# Revit family: PRD_AR_FlshCntrlDvcs_F5EElectronicWCFlush_F5EF4004
name_source: partatom
category: Plumbing Fixtures
units: mm (PartAtom-declared; Revit-internal decimal feet)

## family parameters
Cut with Voids When Loaded = Yes
Enable Cutting in Views = Yes
Host = Face
Maintain Annotation Orientation = No
OmniClass Number = 23.45.55.11
OmniClass Title = Sanitary Components
Part Type = Normal
Room Calculation Point = No
Round Connector Dimension = Use Diameter
Shared = No

## types (1)
- F5EF4004
    AssetType = Fixed
    BIMObjectName = PRD_AR_FlushControlDevices_F5EElectronicWCFlush_F5EF4004
    BasicColour = stainless steel-look
    BodyMaterial = PRD_AR_StainlessSteel_Brushed
    ButtonMaterial = PRD_AR_ChromatedBrass_HighPolished
    CW Connection = Yes
    CWFU = 0
    Category = Pr_75_50_46_31, Flush control devices
    Color = stainless steel-look
    Default Elevation = 1219 mm
    DefaultAutomaticHygieneFlush = 24h after the last activity
    Description = F5E - A3000 open WC flush valve for concealed mounting, electronically controlled. Especially suitable for facilities at risk of vandalism. With waterproof electronic module with additional input for sensors to be provided by the client, maximum distance to the electronic module 5 m, solenoid flush valve including enclosed throttle insert for reducing flush volume, waterproof electrical T-junction for connection to system cable, stainless steel cover plate 190 x 245 x 2 mm for invisible mounting via threaded rods, up to a wall thickness of 50 to 500 mm, including piezo push-button and 2 m extension cable. Activated hygiene flushing 24 hours after the last activity. With facility for parameterization, cleaning deactivation and communication via ECC2 function controller, 24 V DC.
    DiameterNominal = DN 20
    Export Type to IFC As = IfcSensorType
    Features = Stainless steel cover plate 190 x 245 x 2 mm for invisible mounting via threaded rods, up to a wall thickness of 50 to 500 mm.
    Finish = Satin finished
    FlushingVolumeAdjustable = Yes
    FunctionalPrinciple = electronic self-closing
    HW Connection = Yes
    HWFU = 0
    HygieneFlushing = Yes
    IfcExportAs = IfcSensorType
    IfcExportType = USERDEFINED
    Manufacturer = KWC Group Management AG
    ManufacturerName = KWC Group Management AG
    ManufacturerURL = www.kwc-professional.com
    MateriaFitting = brass-look
    Material = Stainless steel
    MaterialCasing = stainless steel
    MaterialCodeCasing = 1.4301 Chrome Nickel steel V2A
    MaximumFlowPressure = 4 bar
    MaximumFlushWaterVolume = 9 Liter
    MaximumFlushingFlow = 1 l/s
    MinimumFlowPressure = 1.2 bar
    MinimumFlushWaterVolume = 6 Liter
    Model = F5EF4004
    ModelNumber = 2030068198
    ModelReference = F5EF4004
    NBSDescription = Flush control devices
    NBSReference = 90-15-35/470
    Name = F5E Electronic WC flush F5EF4004
    NominalDepth = 2 mm  [stored 0.00656168 ft]
    NominalHeight = 245 mm  [stored 0.803806 ft]
    NominalWidth = 190 mm
    Parameterization = network
    PowerConsumption = 2.5 Voltampere
    PowerSupplyConnection = A3000 open 24 V DC
    ProductInformation = http://pim.kwc.com
    ProtectiveShutdown = Yes
    ProtectiveSystemIP = IP59K
    Size = 20
    SoundInsulation = No
    Status = New
    SurfaceFinishCasing = satin finished
    Type IFC Predefined Type = USERDEFINED
    TypeOfFlushingFitting = WC flush valve
    TypeOfMounting = concealed
    TypeOfOperation = sensor operation
    TypeOfPowerSupply = Transformer
    TypeOfSensor = piezo-electronic sensor
    URL = www.kwc-professional.com
    Uniclass2015Code = Pr_75_50_46_31
    Uniclass2015Title = Flush control devices
    Uniclass2015Version = Products v1.36
    Vent Connection = Yes
    Version = 1
    WFU = 0
    Waste Connection = Yes
    WithTransformerPowerSupply = No

note: [stored X ft] marks values corroborated as IEEE doubles in the binary element streams (Revit-internal decimal feet)

## geometry (parser evidence)
native form markers: Sweep x5
no freeform markers — native parametric forms only
